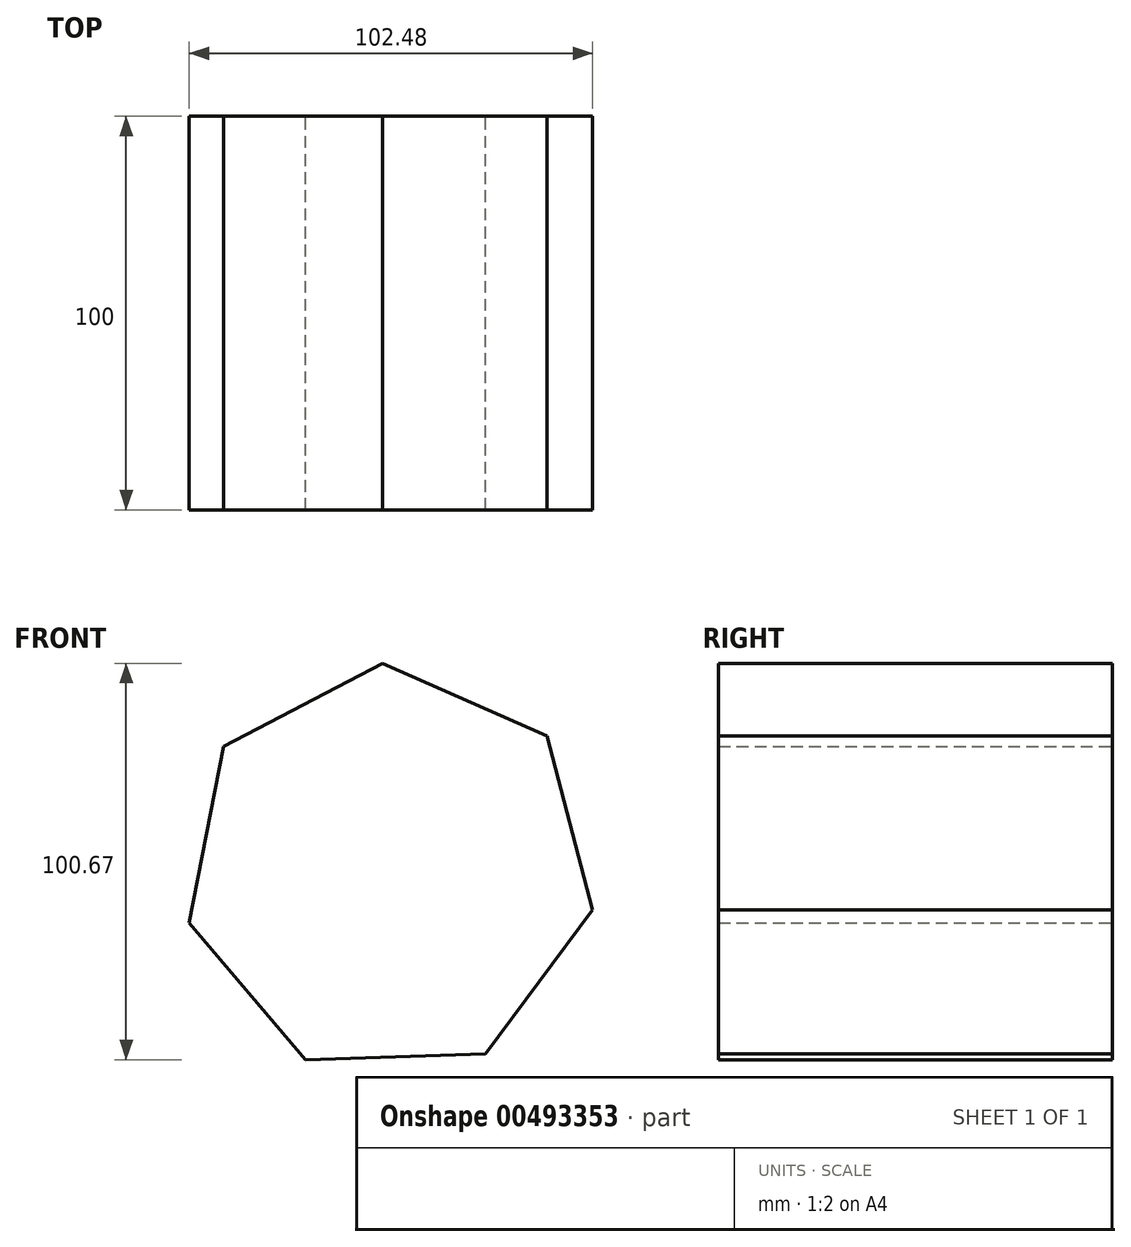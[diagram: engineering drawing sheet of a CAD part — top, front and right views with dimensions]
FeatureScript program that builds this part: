
annotation { "Feature Type Name" : "Feature", "Feature Type Description" : "" }
export const myFeature = defineFeature(function(context is Context, id is Id, definition is map)
    precondition{}
    {
        {
            var Q0;
            Q0=qCreatedBy(makeId("Front.planeOp"),FACE);
            var sketch = newSketch(context, id + "F0", { "sketchPlane" : qUnion([Q0])});
            skCircle(sketch, "E0.cCircle", {"center": v(0, 0) * mm, "radius": 52.59 * mm, "construction": true});
            skLineSegment(sketch, "E0.0", {"start": v(-42.17, 31.41) * mm, "end": v(-1.73, 52.56) * mm});
            skLineSegment(sketch, "E0.1", {"start": v(-1.73, 52.56) * mm, "end": v(40.01, 34.12) * mm});
            skLineSegment(sketch, "E0.2", {"start": v(40.01, 34.12) * mm, "end": v(51.63, -10) * mm});
            skLineSegment(sketch, "E0.3", {"start": v(51.63, -10) * mm, "end": v(24.37, -46.6) * mm});
            skLineSegment(sketch, "E0.4", {"start": v(24.37, -46.6) * mm, "end": v(-21.24, -48.1) * mm});
            skLineSegment(sketch, "E0.5", {"start": v(-21.24, -48.1) * mm, "end": v(-50.85, -13.39) * mm});
            skLineSegment(sketch, "E0.6", {"start": v(-50.85, -13.39) * mm, "end": v(-42.17, 31.41) * mm});
            skSolve(sketch);
        }
        {
            var Q0;
            Q0 = qSketchRegion(id + "F0", true);
            extrude(context, id + "F1", {"entities" : qUnion([Q0]), "endBound" : BoundingType.SYMMETRIC, "depth" : 100 * mm});
        }
    });
